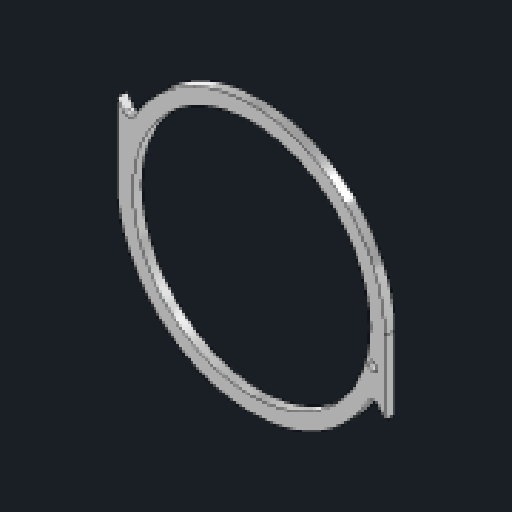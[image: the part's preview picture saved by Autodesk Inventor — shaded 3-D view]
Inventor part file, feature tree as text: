
AUTODESK INVENTOR PART (.ipt)
format: ipt  version: 2023.2 (Build 272271030, 271C)  size: 130,560 bytes
history: native  units: mm
features: sketch x2, extrude x1, hole x1, pattern_circular x1
ambient origin geometry x8: Origin, YZ Plane, XZ Plane, XY Plane, X Axis, Y Axis, Z Axis, Center Point
bodies: Solid1 (feature_tree)
feature tree (5):
  extrude  "Extrusion1"  Depth=8.0mm
  hole  "Hole1"  [1 undecoded]
  pattern_circular  "Circular Pattern1"  [2 undecoded]
  sketch  "Sketch1"  dims[d0=127.0mm d1=8.0mm]
  sketch  "Sketch2"  dims[d2=5.0mm d3=0.0mm d4=10.0mm d5=3.1mm d6=20.0mm d8=360.0deg d10=67.5mm d11=165.0deg d12=4.7625mm d13=6.0mm d14=4.0mm d15=2.0mm d16=90.0deg d17=3.5mm d18=0.0mm d19=60.0mm d20=360.0deg]
note: 3 required parameter values undecoded (feature->parameter linkage not recoverable at this tier; creation-order binding heuristic only, values carry confidence <= 0.55)
